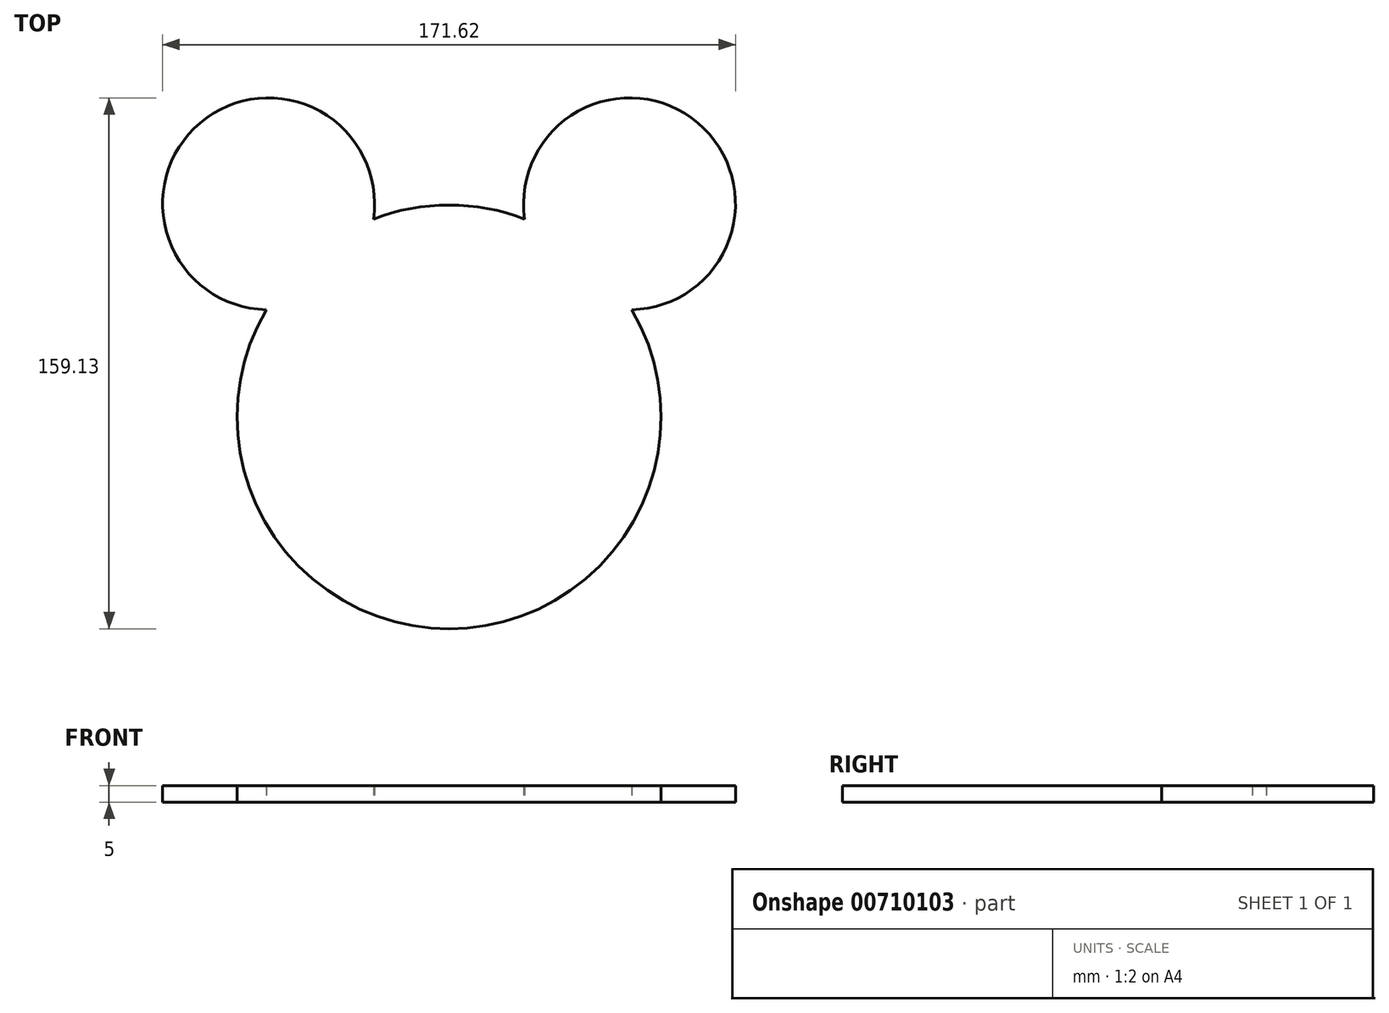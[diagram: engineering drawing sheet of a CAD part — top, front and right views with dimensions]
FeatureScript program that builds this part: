
annotation { "Feature Type Name" : "Feature", "Feature Type Description" : "" }
export const myFeature = defineFeature(function(context is Context, id is Id, definition is map)
    precondition{}
    {
        {
            var Q0;
            Q0=qCreatedBy(makeId("Top.planeOp"),FACE);
            var sketch = newSketch(context, id + "F0", { "sketchPlane" : qUnion([Q0])});
            skArc(sketch, "E0", {"start": v(-54.77, 32.14) * mm, "mid": v(0, -63.5) * mm, "end": v(54.77, 32.14) * mm});
            skLineSegment(sketch, "E1", {"start": v(0, 0) * mm, "end": v(-54.06, 63.88) * mm, "construction": true});
            skLineSegment(sketch, "E2", {"start": v(54.06, 63.88) * mm, "end": v(0, 0) * mm, "construction": true});
            skArc(sketch, "E3", {"start": v(-22.64, 59.33) * mm, "mid": v(-74.57, 88.12) * mm, "end": v(-54.77, 32.14) * mm});
            skArc(sketch, "E4", {"start": v(54.77, 32.14) * mm, "mid": v(74.57, 88.12) * mm, "end": v(22.64, 59.33) * mm});
            skArc(sketch, "E5.trimOffspring", {"start": v(22.64, 59.33) * mm, "mid": v(0, 63.5) * mm, "end": v(-22.64, 59.33) * mm});
            skCircle(sketch, "E6", {"center": v(-1.08, 28.48) * mm, "radius": 101.6 * mm, "construction": true});
            skSolve(sketch);
        }
        {
            var Q0;
            Q0 = qSketchRegion(id + "F0", true);
            extrude(context, id + "F1", {"entities" : qUnion([Q0]), "depth" : 5 * mm, "offsetDistance" : 25.4 * mm});
        }
    });
